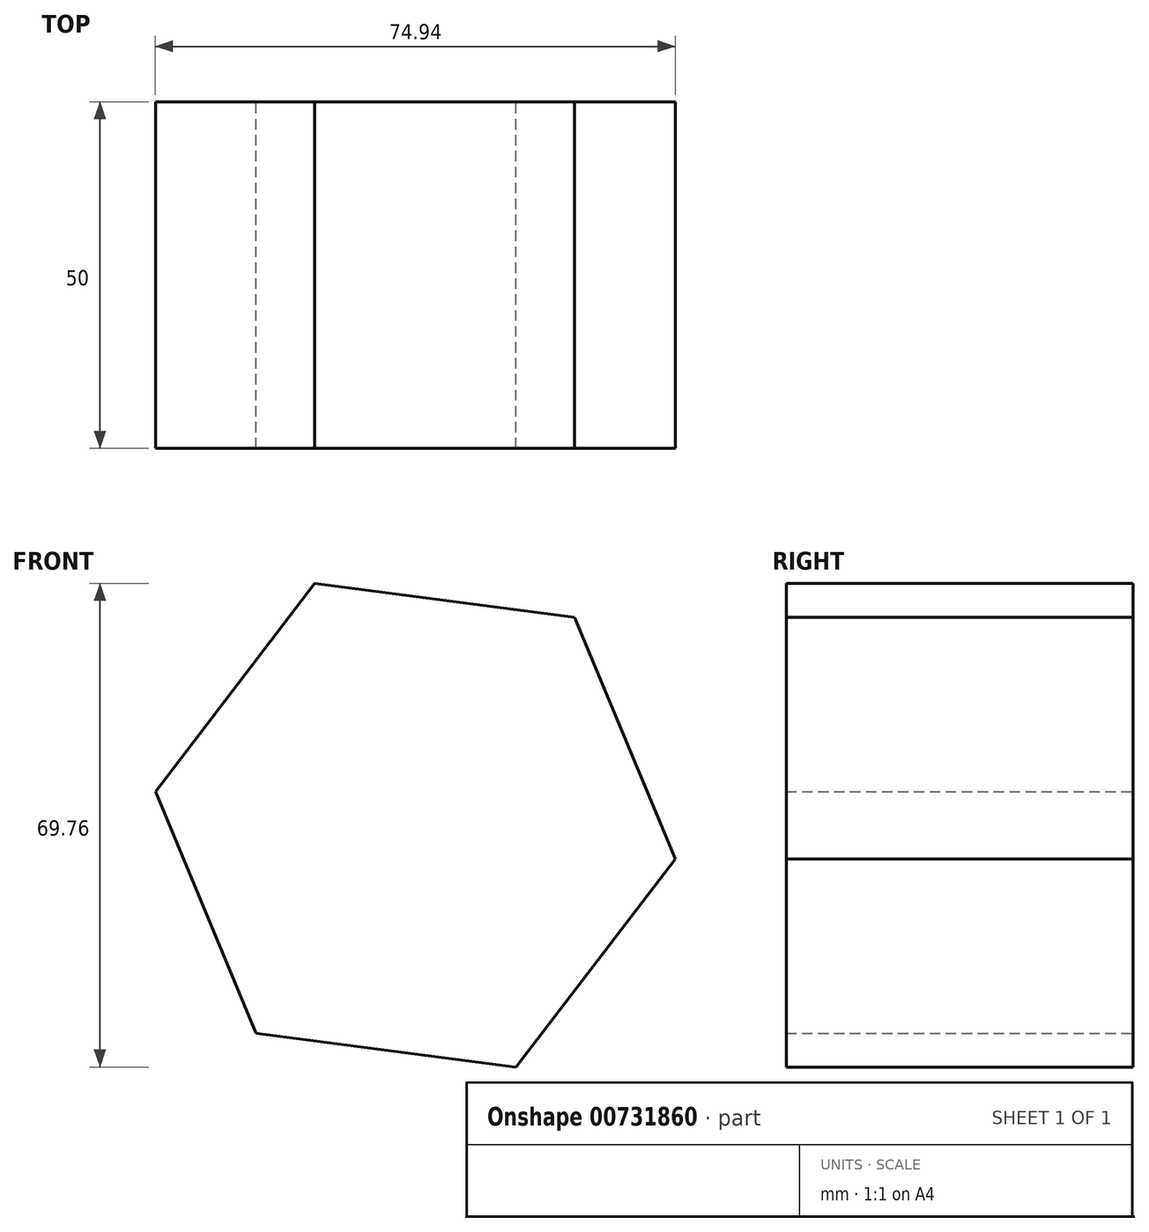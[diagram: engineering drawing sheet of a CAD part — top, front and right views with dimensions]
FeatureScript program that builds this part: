
annotation { "Feature Type Name" : "Feature", "Feature Type Description" : "" }
export const myFeature = defineFeature(function(context is Context, id is Id, definition is map)
    precondition{}
    {
        {
            var Q0;
            Q0=qCreatedBy(makeId("Front.planeOp"),FACE);
            var sketch = newSketch(context, id + "F0", { "sketchPlane" : qUnion([Q0])});
            skCircle(sketch, "E0.cCircle", {"center": v(0, 0) * mm, "radius": 32.72 * mm, "construction": true});
            skLineSegment(sketch, "E0.0", {"start": v(22.95, 30.01) * mm, "end": v(37.47, -4.87) * mm});
            skLineSegment(sketch, "E0.1", {"start": v(37.47, -4.87) * mm, "end": v(14.52, -34.88) * mm});
            skLineSegment(sketch, "E0.2", {"start": v(14.52, -34.88) * mm, "end": v(-22.95, -30.01) * mm});
            skLineSegment(sketch, "E0.3", {"start": v(-22.95, -30.01) * mm, "end": v(-37.47, 4.87) * mm});
            skLineSegment(sketch, "E0.4", {"start": v(-37.47, 4.87) * mm, "end": v(-14.52, 34.88) * mm});
            skLineSegment(sketch, "E0.5", {"start": v(-14.52, 34.88) * mm, "end": v(22.95, 30.01) * mm});
            skPoint(sketch, "E0.0.midPoint", {"position": v(30.2, 12.57) * mm});
            skSolve(sketch);
        }
        {
            var Q0;
            Q0=makeQuery(id+"F0.imprint","IMPRINT",FACE,{"disambiguationData":[TD([[makeQuery(id+"F0.imprint","IMPRINT",EDGE,{"derivedFrom":sQuery(id+"F0.wireOp",EDGE,"E0.0")}),-1.0]])]});
            extrude(context, id + "F1", {"entities" : qUnion([Q0]), "endBound" : BoundingType.SYMMETRIC, "depth" : 50 * mm, "offsetDistance" : 25 * mm});
        }
    });
